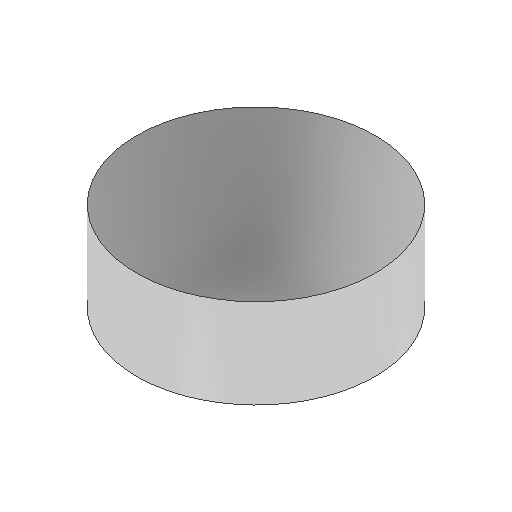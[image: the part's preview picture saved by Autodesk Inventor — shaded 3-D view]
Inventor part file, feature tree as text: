
AUTODESK INVENTOR PART (.ipt)
format: ipt  version: 2022 (Build 260153000, 153)  size: 97,792 bytes
history: native  units: mm
features: extrude x1, sketch x1
ambient origin geometry x8: Origin, YZ Plane, XZ Plane, XY Plane, X Axis, Y Axis, Z Axis, Center Point
bodies: Volumenkörper1 (feature_tree)
feature tree (2):
  extrude  "Extrusion1"  Depth=3.0mm TaperAngle=0.0deg
  sketch  "Skizze1"  dims[d0=8.0mm d1=3.0mm d2=0.0mm]
